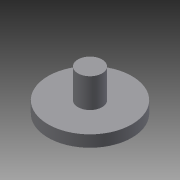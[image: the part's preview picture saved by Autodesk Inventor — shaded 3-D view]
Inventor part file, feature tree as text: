
AUTODESK INVENTOR PART (.ipt)
format: ipt  version: 2013 (Build 170138000, 138)  size: 74,752 bytes
history: native  units: mm
features: extrude x2, sketch x2, other x1
ambient origin geometry x8: Origin, YZ Plane, XZ Plane, XY Plane, X Axis, Y Axis, Z Axis, Center Point
feature tree (5):
  other  "ソリッド1"
  extrude  "押し出し1"  Depth=16.6mm
  extrude  "押し出し2"  Depth=2.3mm TaperAngle=0.0deg
  sketch  "スケッチ1"
  sketch  "スケッチ2"
